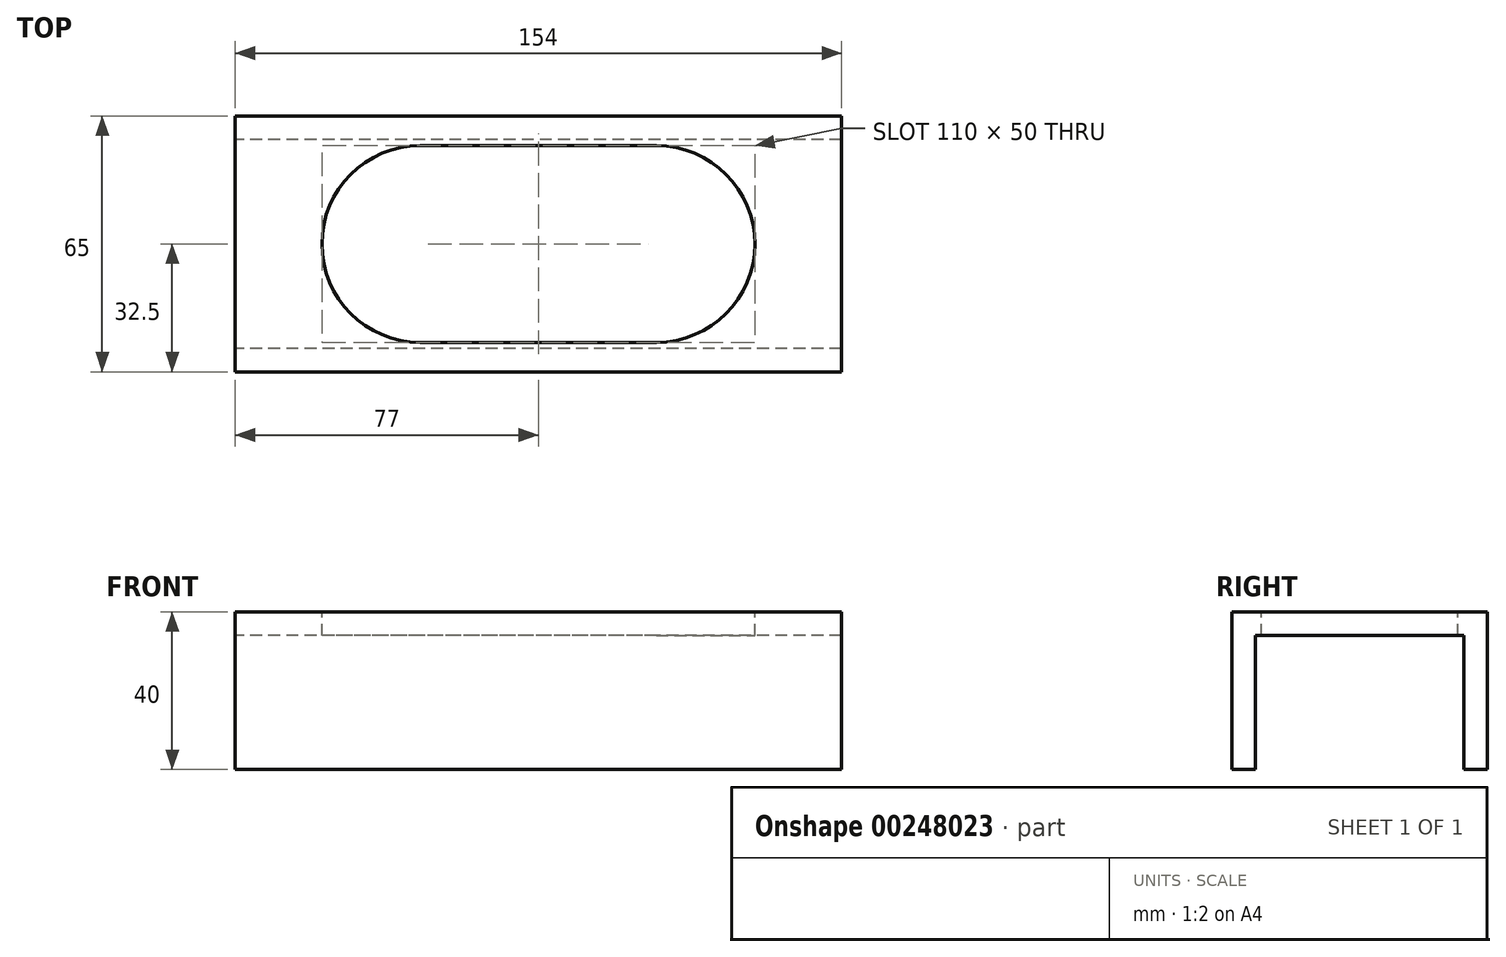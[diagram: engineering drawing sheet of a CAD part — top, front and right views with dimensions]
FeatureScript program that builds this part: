
annotation { "Feature Type Name" : "Feature", "Feature Type Description" : "" }
export const myFeature = defineFeature(function(context is Context, id is Id, definition is map)
    precondition{}
    {
        {
            var Q0;
            Q0=qCreatedBy(makeId("Front.planeOp"),FACE);
            var sketch = newSketch(context, id + "F0", { "sketchPlane" : qUnion([Q0])});
            skLineSegment(sketch, "E0.bottom", {"start": v(77, 20) * mm, "end": v(-77, 20) * mm});
            skLineSegment(sketch, "E0.top", {"start": v(77, -20) * mm, "end": v(-77, -20) * mm});
            skLineSegment(sketch, "E0.left", {"start": v(77, 20) * mm, "end": v(77, -20) * mm});
            skLineSegment(sketch, "E0.right", {"start": v(-77, 20) * mm, "end": v(-77, -20) * mm});
            skPoint(sketch, "E0.middle", {"position": v(0, 0) * mm});
            skSolve(sketch);
        }
        {
            var Q0;
            Q0=makeQuery(id+"F0.imprint","IMPRINT",FACE,{"disambiguationData":[TD([[makeQuery(id+"F0.imprint","IMPRINT",EDGE,{"derivedFrom":sQuery(id+"F0.wireOp",EDGE,"E0.bottom")}),1.0]])]});
            extrude(context, id + "F1", {"entities" : qUnion([Q0]), "depth" : 65 * mm, "offsetDistance" : 25 * mm, "symmetric" : true});
        }
        {
            var Q0;
            Q0=makeQuery(id+"F1.opExtrude","SWEPT_FACE",FACE,{"disambiguationData":[OSD([sQuery(id+"F0.wireOp",EDGE,"E0.top")])]});
            var Q1;
            Q1=makeQuery(id+"F1.opExtrude","SWEPT_FACE",FACE,{"disambiguationData":[OSD([sQuery(id+"F0.wireOp",EDGE,"E0.right")])]});
            var Q2;
            Q2=makeQuery(id+"F1.opExtrude","SWEPT_FACE",FACE,{"disambiguationData":[OSD([sQuery(id+"F0.wireOp",EDGE,"E0.left")])]});
            shell(context, id + "F2", {"entities" : qUnion([Q0, Q1, Q2]), "thickness" : 6 * mm});
        }
        {
            var Q0;
            Q0=makeQuery(id+"F1.opExtrude","SWEPT_FACE",FACE,{"disambiguationData":[OSD([sQuery(id+"F0.wireOp",EDGE,"E0.bottom")])]});
            var sketch = newSketch(context, id + "F3", { "sketchPlane" : qUnion([Q0])});
            skPoint(sketch, "E1.middle", {"position": v(0, 0) * mm});
            skArc(sketch, "E2", {"start": v(-30, 25) * mm, "mid": v(-55, 0) * mm, "end": v(-30, -25) * mm});
            skArc(sketch, "E3", {"start": v(30, -25) * mm, "mid": v(55, 0) * mm, "end": v(30, 25) * mm});
            skLineSegment(sketch, "E4", {"start": v(-30, 25) * mm, "end": v(30, 25) * mm});
            skLineSegment(sketch, "E5", {"start": v(30, -25) * mm, "end": v(-30, -25) * mm});
            skSolve(sketch);
        }
        {
            var Q0;
            Q0=makeQuery(id+"F3.imprint","IMPRINT",FACE,{"disambiguationData":[TD([[makeQuery(id+"F3.imprint","IMPRINT",EDGE,{"derivedFrom":sQuery(id+"F3.wireOp",EDGE,"E2")}),1.0]])]});
            extrude(context, id + "F4", {"entities" : qUnion([Q0]), "operationType" : NewBodyOperationType.REMOVE, "oppositeDirection" : true, "depth" : 7 * mm, "offsetDistance" : 25 * mm});
        }
    });
